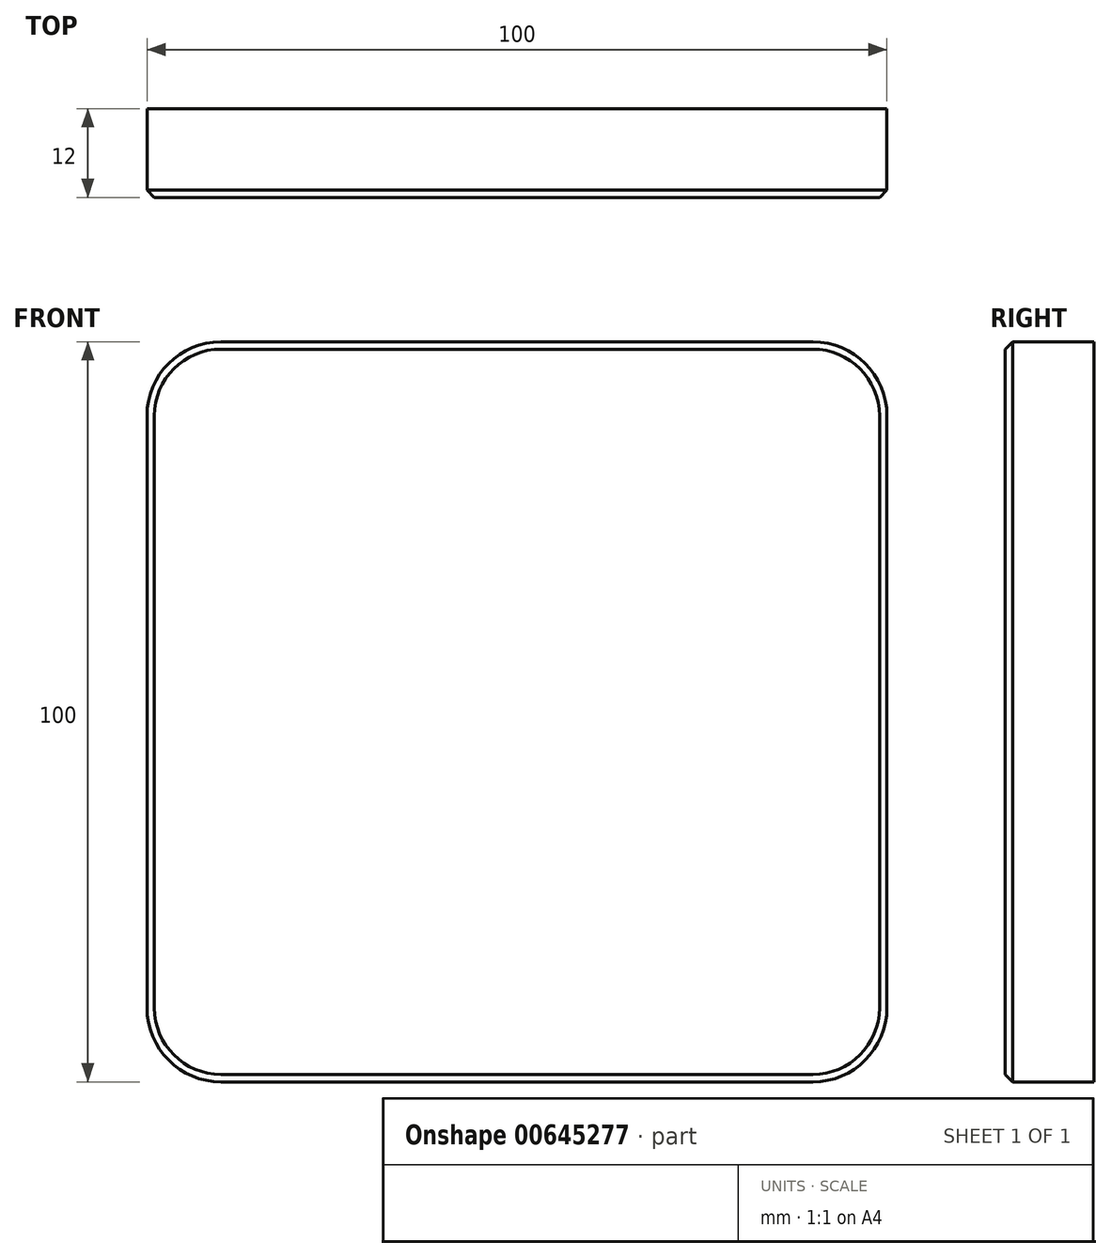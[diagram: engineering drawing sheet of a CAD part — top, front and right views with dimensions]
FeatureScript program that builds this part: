
annotation { "Feature Type Name" : "Feature", "Feature Type Description" : "" }
export const myFeature = defineFeature(function(context is Context, id is Id, definition is map)
    precondition{}
    {
        {
            var Q0;
            Q0=qCreatedBy(makeId("Front.planeOp"),FACE);
            var sketch = newSketch(context, id + "F0", { "sketchPlane" : qUnion([Q0])});
            skLineSegment(sketch, "E0.bottom", {"start": v(40, -50) * mm, "end": v(-40, -50) * mm});
            skLineSegment(sketch, "E0.top", {"start": v(40, 50) * mm, "end": v(-40, 50) * mm});
            skLineSegment(sketch, "E0.left", {"start": v(50, -40) * mm, "end": v(50, 40) * mm});
            skLineSegment(sketch, "E0.right", {"start": v(-50, -40) * mm, "end": v(-50, 40) * mm});
            skPoint(sketch, "E0.middle", {"position": v(0, 0) * mm});
            skPoint(sketch, "E1.visualSharp", {"position": v(-50, 50) * mm});
            skArc(sketch, "E1.filletArc", {"start": v(-40, 50) * mm, "mid": v(-47.07, 47.07) * mm, "end": v(-50, 40) * mm});
            skPoint(sketch, "E2.visualSharp", {"position": v(50, 50) * mm});
            skArc(sketch, "E2.filletArc", {"start": v(50, 40) * mm, "mid": v(47.07, 47.07) * mm, "end": v(40, 50) * mm});
            skPoint(sketch, "E3.visualSharp", {"position": v(50, -50) * mm});
            skArc(sketch, "E3.filletArc", {"start": v(40, -50) * mm, "mid": v(47.07, -47.07) * mm, "end": v(50, -40) * mm});
            skPoint(sketch, "E4.visualSharp", {"position": v(-50, -50) * mm});
            skArc(sketch, "E4.filletArc", {"start": v(-50, -40) * mm, "mid": v(-47.07, -47.07) * mm, "end": v(-40, -50) * mm});
            skSolve(sketch);
        }
        {
            var Q0;
            Q0 = qSketchRegion(id + "F0", true);
            extrude(context, id + "F1", {"entities" : qUnion([Q0]), "depth" : 12 * mm, "offsetDistance" : 25 * mm});
        }
        {
            var Q0;
            Q0=makeQuery(id+"F1.opExtrude","CAP_EDGE",EDGE,{"disambiguationData":[OSD([sQuery(id+"F0.wireOp",EDGE,"E0.bottom")])],"isStart":false});
            var Q1;
            Q1=makeQuery(id+"F1.opExtrude","CAP_EDGE",EDGE,{"disambiguationData":[OSD([sQuery(id+"F0.wireOp",EDGE,"E4.filletArc")])],"isStart":false});
            chamfer(context, id + "F2", {"entities" : qUnion([Q0, Q1]), "chamferType" : ChamferType.OFFSET_ANGLE, "width" : 1 * mm, "oppositeDirection" : false, "angle" : 45 * degree, "tangentPropagation" : true});
        }
    });
